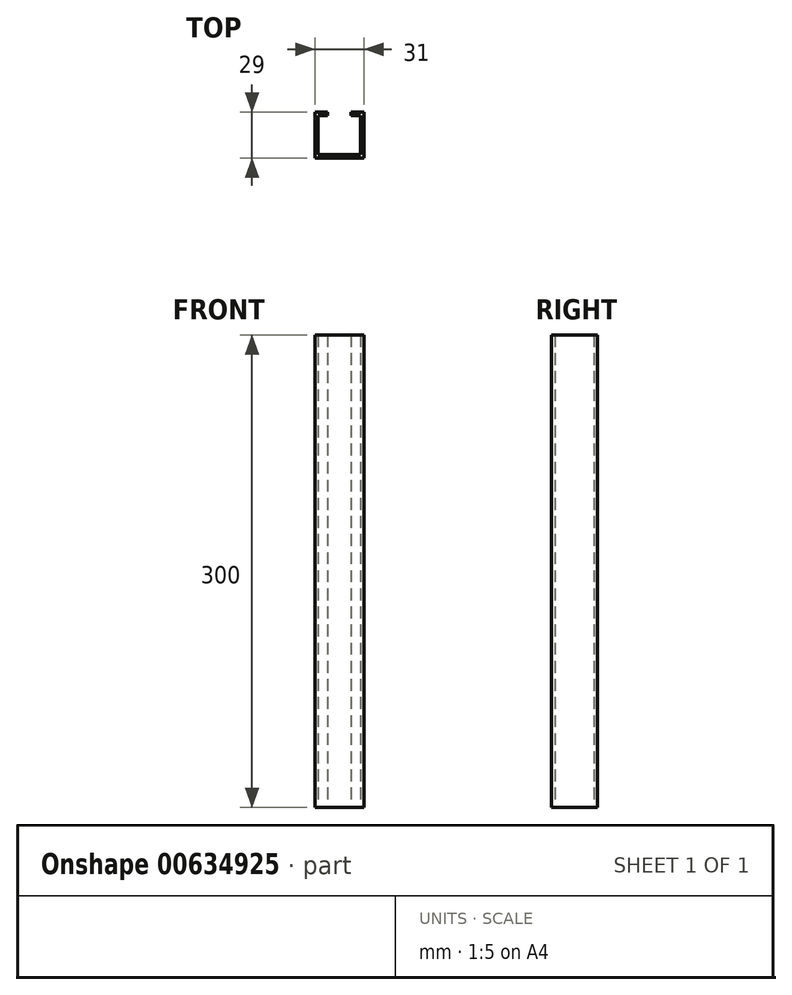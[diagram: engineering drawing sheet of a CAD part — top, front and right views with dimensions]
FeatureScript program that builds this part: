
annotation { "Feature Type Name" : "Feature", "Feature Type Description" : "" }
export const myFeature = defineFeature(function(context is Context, id is Id, definition is map)
    precondition{}
    {
        {
            var Q0;
            Q0=qCreatedBy(makeId("Top.planeOp"),FACE);
            var sketch = newSketch(context, id + "F0", { "sketchPlane" : qUnion([Q0])});
            skLineSegment(sketch, "E0", {"start": v(-15.5, 0) * mm, "end": v(15.5, 0) * mm});
            skLineSegment(sketch, "E1", {"start": v(15.5, 0) * mm, "end": v(15.5, 29) * mm});
            skLineSegment(sketch, "E2", {"start": v(15.5, 29) * mm, "end": v(7.5, 29) * mm});
            skLineSegment(sketch, "E3", {"start": v(-15.5, 0) * mm, "end": v(-15.5, 29) * mm});
            skLineSegment(sketch, "E4", {"start": v(-15.5, 29) * mm, "end": v(-7.5, 29) * mm});
            skLineSegment(sketch, "E5", {"start": v(-7.5, 29) * mm, "end": v(-7.5, 27) * mm});
            skLineSegment(sketch, "E6", {"start": v(-7.5, 27) * mm, "end": v(-13.5, 27) * mm});
            skLineSegment(sketch, "E7", {"start": v(-13.5, 27) * mm, "end": v(-13.5, 2) * mm});
            skLineSegment(sketch, "E8", {"start": v(-13.5, 2) * mm, "end": v(13.5, 2) * mm});
            skLineSegment(sketch, "E9", {"start": v(13.5, 2) * mm, "end": v(13.5, 27) * mm});
            skLineSegment(sketch, "E10", {"start": v(13.5, 27) * mm, "end": v(7.48, 27) * mm});
            skLineSegment(sketch, "E11", {"start": v(7.48, 27) * mm, "end": v(7.5, 29) * mm});
            skSolve(sketch);
        }
        {
            var Q0;
            Q0 = qSketchRegion(id + "F0", true);
            extrude(context, id + "F1", {"entities" : qUnion([Q0]), "depth" : 300 * mm, "offsetDistance" : 25 * mm});
        }
    });
